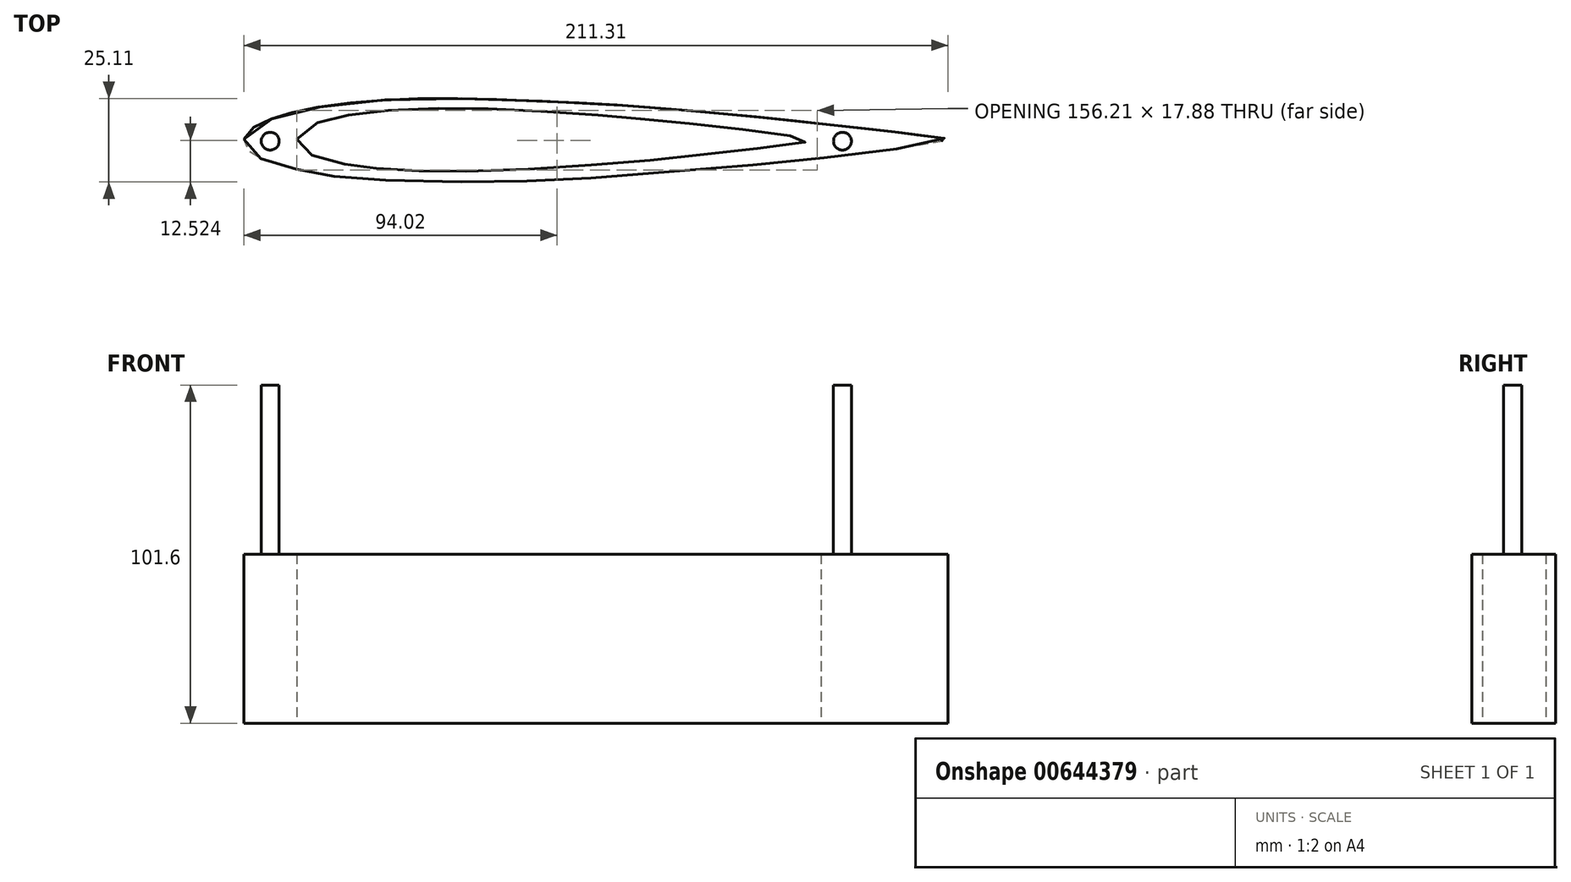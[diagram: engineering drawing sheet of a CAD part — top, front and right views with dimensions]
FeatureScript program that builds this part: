
annotation { "Feature Type Name" : "Feature", "Feature Type Description" : "" }
export const myFeature = defineFeature(function(context is Context, id is Id, definition is map)
    precondition{}
    {
        {
            var Q0;
            Q0=qCreatedBy(makeId("Top.planeOp"),FACE);
            var sketch = newSketch(context, id + "F0", { "sketchPlane" : qUnion([Q0])});
            skFitSpline(sketch, "E0", {"points": [v(-119.16, 2.2) * mm, v(-117.58, 4.8) * mm, v(-114.1, 7.05) * mm, v(-108.14, 9.27) * mm, v(-101.61, 10.98) * mm, v(-88.34, 13) * mm, v(-74.4, 14.13) * mm, v(-54.26, 14.47) * mm, v(-33, 13.8) * mm, v(-10.18, 12.67) * mm, v(5.34, 11.55) * mm, v(23.9, 9.97) * mm, v(39.34, 8.43) * mm, v(58.37, 6.42) * mm, v(70.85, 4.98) * mm, v(81.75, 3.63) * mm, v(86.76, 2.92) * mm, v(92.09, 2.2) * mm, v(81.43, -0.03) * mm, v(64.9, -2.25) * mm, v(44.77, -4.48) * mm, v(29.58, -5.83) * mm, v(4.69, -7.82) * mm, v(-14.95, -9.41) * mm, v(-29.67, -10.13) * mm, v(-40.72, -10.44) * mm, v(-57.58, -10.6) * mm, v(-76.43, -10.13) * mm, v(-86.59, -9.57) * mm, v(-93.85, -8.7) * mm, v(-99.5, -7.74) * mm, v(-102.6, -7.02) * mm, v(-107.92, -5.75) * mm, v(-112.38, -4.24) * mm, v(-114.92, -3.2) * mm, v(-117.15, -1.86) * mm, v(-118.82, 0.05) * mm, v(-119.16, 2.2) * mm]});
            skFitSpline(sketch, "E1", {"points": [v(-103.3, 2.2) * mm, v(-103.11, 3.13) * mm, v(-102.27, 4.4) * mm, v(-100.06, 6) * mm, v(-98.12, 6.9) * mm, v(-96.43, 7.48) * mm, v(-94.7, 8) * mm, v(-91.69, 8.76) * mm, v(-89.54, 9.2) * mm, v(-85.86, 9.82) * mm, v(-83.29, 10.17) * mm, v(-79.65, 10.58) * mm, v(-73.26, 11.04) * mm, v(-66.87, 11.36) * mm, v(-61.14, 11.48) * mm, v(-55.92, 11.55) * mm, v(-49.73, 11.43) * mm, v(-43, 11.25) * mm, v(-36.6, 10.97) * mm, v(-29.22, 10.56) * mm, v(-21.86, 10.12) * mm, v(-13.03, 9.48) * mm, v(-9.49, 9.18) * mm, v(-4.38, 8.74) * mm, v(0, 8.37) * mm, v(4.87, 7.91) * mm, v(12.02, 7.15) * mm, v(17.67, 6.57) * mm, v(26.42, 5.57) * mm, v(31.46, 5.01) * mm, v(37.25, 4.3) * mm, v(43.04, 3.52) * mm, v(48.24, 2.87) * mm, v(54.03, 2.2) * mm, v(48.99, 1.3) * mm, v(43.75, 0.56) * mm, v(37.74, -0.26) * mm, v(32.17, -0.84) * mm, v(25.05, -1.72) * mm, v(17.34, -2.53) * mm, v(9.83, -3.35) * mm, v(3.23, -4.03) * mm, v(-4.16, -4.71) * mm, v(-13.3, -5.44) * mm, v(-22.67, -6.1) * mm, v(-32.36, -6.75) * mm, v(-44, -7.2) * mm, v(-51.86, -7.45) * mm, v(-57.17, -7.48) * mm, v(-62.72, -7.43) * mm, v(-67.75, -7.28) * mm, v(-71.97, -7.1) * mm, v(-76.9, -6.76) * mm, v(-80.55, -6.43) * mm, v(-82.88, -6.15) * mm, v(-84.96, -5.94) * mm, v(-87.8, -5.5) * mm, v(-90.31, -5.02) * mm, v(-92.97, -4.42) * mm, v(-95.73, -3.72) * mm, v(-98.48, -2.71) * mm, v(-100.65, -1.64) * mm, v(-101.88, -0.7) * mm, v(-102.92, 0.59) * mm, v(-103.24, 1.45) * mm, v(-103.3, 1.87) * mm, v(-103.3, 2.2) * mm]});
            skSolve(sketch);
        }
        {
            var Q0;
            Q0=makeQuery(id+"F0.imprint","IMPRINT",FACE,{"disambiguationData":[TD([[makeQuery(id+"F0.imprint","IMPRINT",EDGE,{"derivedFrom":sQuery(id+"F0.wireOp",EDGE,"E0")}),-1.0]])]});
            extrude(context, id + "F1", {"entities" : qUnion([Q0]), "depth" : 50.8 * mm, "offsetDistance" : 25.4 * mm});
        }
        {
            var Q0;
            Q0=makeQuery(id+"F1.opExtrude","CAP_FACE",FACE,{"disambiguationData":[OSD([sQuery(id+"F0.wireOp",EDGE,"E0"),sQuery(id+"F0.wireOp",EDGE,"E1")])],"isStart":false});
            var sketch = newSketch(context, id + "F2", { "sketchPlane" : qUnion([Q0])});
            skCircle(sketch, "E2", {"center": v(-111.32, 1.64) * mm, "radius": 2.69 * mm});
            skCircle(sketch, "E3", {"center": v(60.44, 1.64) * mm, "radius": 2.69 * mm});
            skSolve(sketch);
        }
        {
            var Q0;
            Q0=makeQuery(id+"F2.imprint","IMPRINT",FACE,{"disambiguationData":[TD([[makeQuery(id+"F2.imprint","IMPRINT",EDGE,{"derivedFrom":sQuery(id+"F2.wireOp",EDGE,"E2")}),1.0]])]});
            var Q1;
            Q1=makeQuery(id+"F2.imprint","IMPRINT",FACE,{"disambiguationData":[TD([[makeQuery(id+"F2.imprint","IMPRINT",EDGE,{"derivedFrom":sQuery(id+"F2.wireOp",EDGE,"E3")}),1.0]])]});
            extrude(context, id + "F3", {"entities" : qUnion([Q0, Q1]), "operationType" : NewBodyOperationType.ADD, "depth" : 50.8 * mm, "offsetDistance" : 25.4 * mm});
        }
    });
